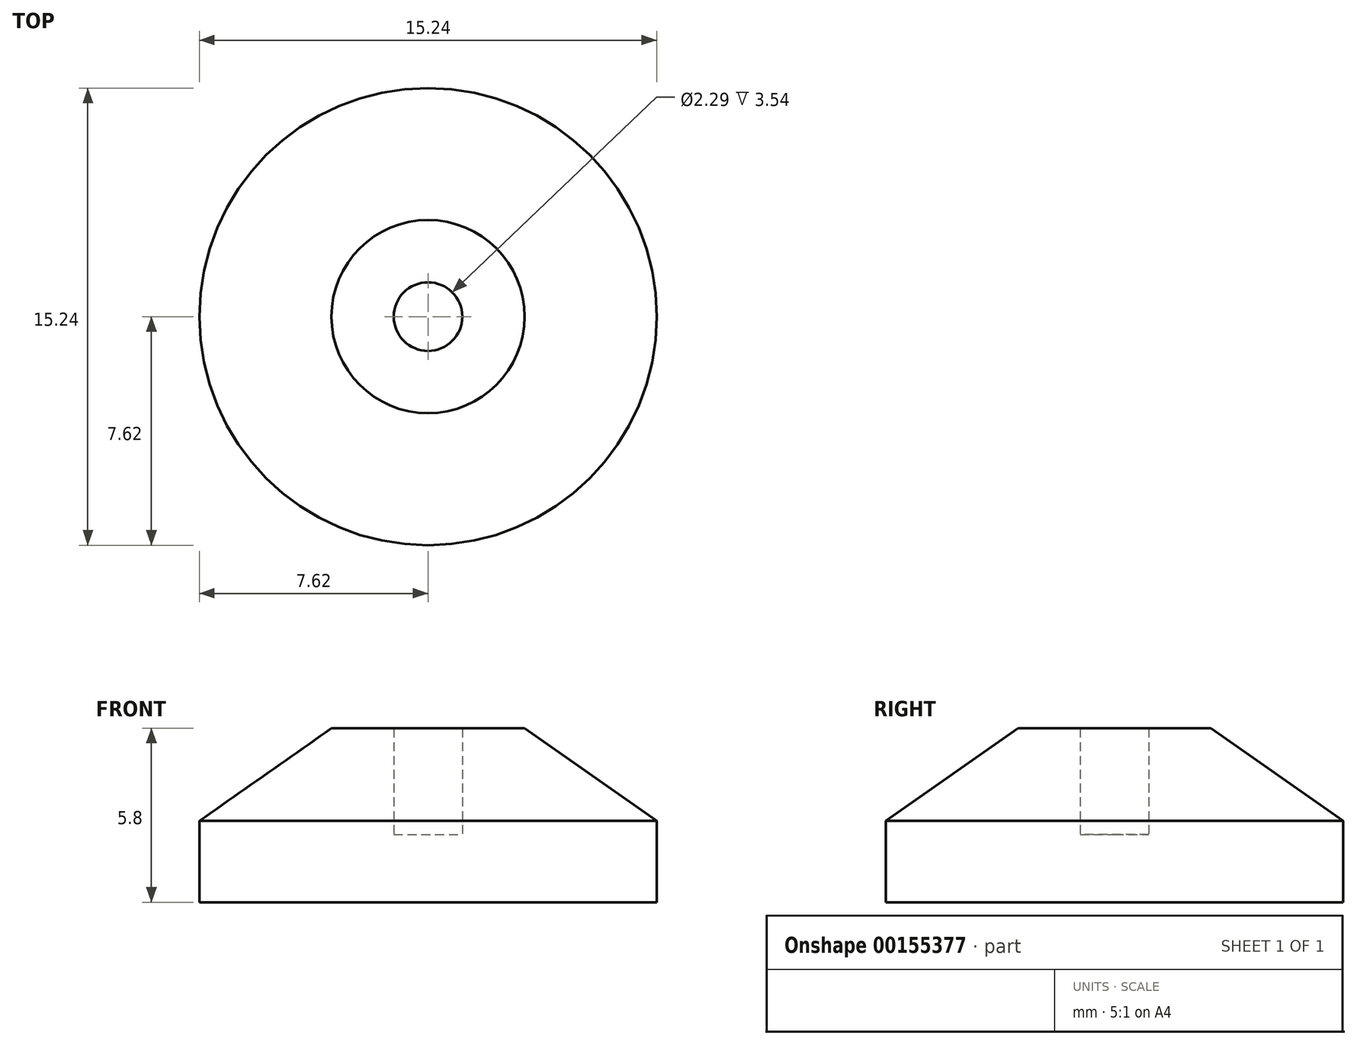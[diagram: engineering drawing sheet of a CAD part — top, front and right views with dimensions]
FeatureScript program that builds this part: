
annotation { "Feature Type Name" : "Feature", "Feature Type Description" : "" }
export const myFeature = defineFeature(function(context is Context, id is Id, definition is map)
    precondition{}
    {
        {
            var Q0;
            Q0=qCreatedBy(makeId("Front.planeOp"),FACE);
            var sketch = newSketch(context, id + "F0", { "sketchPlane" : qUnion([Q0])});
            skLineSegment(sketch, "E0", {"start": v(0, 0) * mm, "end": v(0, 1.5) * mm});
            skLineSegment(sketch, "E1", {"start": v(0, 1.5) * mm, "end": v(1.14, 1.5) * mm});
            skLineSegment(sketch, "E2", {"start": v(1.14, 1.5) * mm, "end": v(1.14, 5.05) * mm});
            skLineSegment(sketch, "E3", {"start": v(1.14, 5.05) * mm, "end": v(3.22, 5.05) * mm});
            skLineSegment(sketch, "E4", {"start": v(3.22, 5.05) * mm, "end": v(7.62, 1.96) * mm});
            skLineSegment(sketch, "E5", {"start": v(7.62, 1.96) * mm, "end": v(7.62, -0.75) * mm});
            skArc(sketch, "E6", {"start": v(6.3, -0.75) * mm, "mid": v(3.18, -0.19) * mm, "end": v(0, 0) * mm});
            skLineSegment(sketch, "E7", {"start": v(6.3, -0.75) * mm, "end": v(7.62, -0.75) * mm});
            skLineSegment(sketch, "E8", {"start": v(6.3, -0.75) * mm, "end": v(0, -0.75) * mm});
            skLineSegment(sketch, "E9", {"start": v(0, -0.75) * mm, "end": v(0, 0) * mm});
            skSolve(sketch);
        }
        {
            var Q0;
            Q0=makeQuery(id+"F0.imprint","IMPRINT",FACE,{"disambiguationData":[TD([[makeQuery(id+"F0.imprint","IMPRINT",EDGE,{"derivedFrom":sQuery(id+"F0.wireOp",EDGE,"E0")}),-1.0]])]});
            var Q1;
            Q1=sQuery(id+"F0.wireOp",EDGE,"E0");
            revolve(context, id + "F1", {"entities" : qUnion([Q0]), "axis" : qUnion([Q1]), "revolveType" : RevolveType.FULL});
        }
        {
            var Q0;
            Q0=makeQuery(id+"F0.imprint","IMPRINT",FACE,{"disambiguationData":[TD([[makeQuery(id+"F0.imprint","IMPRINT",EDGE,{"derivedFrom":sQuery(id+"F0.wireOp",EDGE,"E6")}),1.0]])]});
            var Q1;
            Q1=sQuery(id+"F0.wireOp",EDGE,"E0");
            revolve(context, id + "F2", {"operationType" : NewBodyOperationType.ADD, "entities" : qUnion([Q0]), "axis" : qUnion([Q1]), "revolveType" : RevolveType.FULL});
        }
    });
